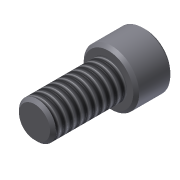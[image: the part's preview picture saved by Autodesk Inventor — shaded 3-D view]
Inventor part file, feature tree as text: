
AUTODESK INVENTOR PART (.ipt)
format: ipt  version: 2011 (Build 150239000, 239)  size: 111,616 bytes
history: native  units: in
note: dims shown in document units (in); Inventor stores cm internally (conversion verified against a paired STEP export)
features: extrude x3, sketch x3, chamfer x1, thread x1
ambient origin geometry x8: Origin, YZ Plane, XZ Plane, XY Plane, X Axis, Y Axis, Z Axis, Center Point
bodies: Solid1 (feature_tree)
feature tree (8):
  extrude  "Extrusion1"  Depth=0.5in TaperAngle=0.0deg
  extrude  "Extrusion2"  Depth=0.25in TaperAngle=0.0deg
  extrude  "Extrusion3"  Depth=0.125in TaperAngle=0.0deg
  chamfer  "Chamfer1"  Distance=0.02in Angle=45.0deg
  thread  "Thread1"  [1 undecoded]
  sketch  "Sketch1"  dims[d0=0.25in d1=0.5in d2=0.0in]
  sketch  "Sketch2"  dims[d3=0.375in d4=0.25in d5=0.0in]
  sketch  "Sketch3"  dims[d6=0.1875in d7=0.125in d8=0.0in d9=0.02in d10=0.125in d11=45.0deg d12=1.0in d13=0.0in]
note: 1 required parameter value undecoded (feature->parameter linkage not recoverable at this tier; creation-order binding heuristic only, values carry confidence <= 0.55)
